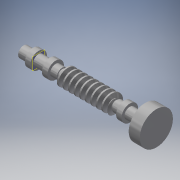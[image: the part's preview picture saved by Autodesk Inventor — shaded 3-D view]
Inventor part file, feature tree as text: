
AUTODESK INVENTOR PART (.ipt)
format: ipt  version: 2019.3 (Build 233278000, 278)  size: 335,360 bytes
history: native  units: mm (DEFAULTED — no unit token found)
features: extrude x8, sketch x8, other x6, plane x3, chamfer x2, pattern_circular x2, mirror x1
ambient origin geometry x6: Origin, XZ Plane, X Axis, Y Axis, Z Axis, Center Point
bodies: Solid1 (feature_tree)
feature tree (30):
  extrude  "Base Body"  Depth=20.29414mm
  chamfer  "Chamfer1"  Distance=3.1425mm
  chamfer  "Chamfer2"  Distance=19.198622mm
  other  "Tooth Sketch"
  other  "Left Tooth"
  pattern_circular  "Left Tooth Pattern"  [2 undecoded]
  other  "Tooth"
  pattern_circular  "Tooth Pattern"  [2 undecoded]
  extrude  "Extrusion3"  Depth=5.700281mm
  extrude  "Extrusion4"  Depth=8.125802mm
  mirror  "Mirror1"
  extrude  "Extrusion5"  Depth=10.248541mm
  plane  "Work Plane10"
  extrude  "Extrusion6"  Depth=6.35mm
  plane  "Work Plane11"
  extrude  "Extrusion7"  Depth=10.0mm
  extrude  "Extrusion8"  Depth=10.0mm
  plane  "Work Plane12"
  extrude  "Extrusion9"  TaperAngle=360.0deg  [1 undecoded]
  other  "Base Body Sketch"
  sketch  "Sketch5"  dims[d4=40.0mm d5=20.29414mm]
  other  "Srf1"
  sketch  "Sketch10"  dims[d6=60.0mm]
  sketch  "Sketch11"  dims[d7=0.0mm]
  sketch  "Sketch12"  dims[d8=1.618499mm]
  sketch  "Sketch15"  dims[d9=4.446789mm]
  sketch  "Sketch16"  dims[d10=1.618499mm]
  sketch  "Sketch17"  dims[d11=4.446789mm]
  sketch  "Sketch18"  dims[d12=19.198622mm d14=3.1425mm d24=19.198622mm d25=34.925mm d26=1.5875mm d27=5.700281mm d28=8.125802mm d29=10.248541mm d30=6.35mm d31=10.0mm d32=120.0mm d33=0.0mm d34=90.0deg d35=90.0deg d36=0.0mm d37=0.0mm d43=10.0mm d45=360.0deg d46=45.0deg d47=45.0deg d49=0.0mm d53=0.0mm d54=58.657497mm d55=0.0mm d56=0.0mm d57=16.251605mm d58=25.4mm d59=0.0mm d60=6.35mm d61=25.4mm d62=120.0mm d63=0.0mm d64=90.0deg d65=90.0deg d66=0.0mm d67=0.0mm d68=10.0mm d69=10.0mm d70=360.0deg d72=10.0mm d74=10.0mm d75=10.0mm d76=0.0mm d77=58.657497mm d81=10.16mm d82=152.4mm d83=0.0mm d84=12.7mm d85=44.45mm d86=0.0mm d87=38.1mm d88=12.7mm d89=0.0mm d90=-17.2212mm d91=19.05mm d92=6.35mm d93=0.0mm d94=-30.4292mm d95=19.05mm d96=6.35mm d97=0.0mm d98=19.05mm d99=4.5212mm d100=0.0mm d101=17.7292mm d102=19.05mm d103=6.35mm d104=0.0mm]
  other  "Pitch Diameter"
note: 5 required parameter values undecoded (feature->parameter linkage not recoverable at this tier; creation-order binding heuristic only, values carry confidence <= 0.55)
